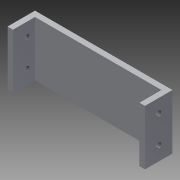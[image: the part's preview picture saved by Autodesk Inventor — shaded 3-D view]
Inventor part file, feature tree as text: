
AUTODESK INVENTOR PART (.ipt)
format: ipt  version: 2013 (Build 170138000, 138)  size: 99,328 bytes
history: native  units: mm
features: thread x4, sketch x2, other x1, extrude x1, hole x1
ambient origin geometry x8: Origin, YZ Plane, XZ Plane, XY Plane, X Axis, Y Axis, Z Axis, Center Point
feature tree (9):
  other  "ソリッド1"
  extrude  "押し出し1"  Depth=50.0mm
  hole  "穴1"  [1 undecoded]
  thread  "ねじ3"
  thread  "ねじ4"
  thread  "ねじ5"
  thread  "ねじ6"
  sketch  "スケッチ1"
  sketch  "スケッチ2"
note: 1 required parameter value undecoded (feature->parameter linkage not recoverable at this tier; creation-order binding heuristic only, values carry confidence <= 0.55)
